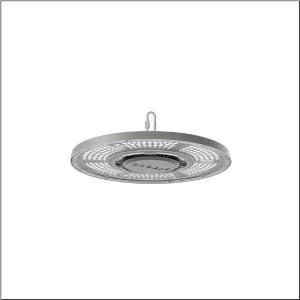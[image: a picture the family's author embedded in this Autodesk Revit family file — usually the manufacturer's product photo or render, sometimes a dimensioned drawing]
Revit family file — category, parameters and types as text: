
# Revit family: highbay_31-s_51hc427a4jmb
name_source: partatom
category: Lighting Fixtures
units: mm (PartAtom-declared; Revit-internal decimal feet)

## family parameters
Cut with Voids When Loaded = No
Host = Face
Light Source = No
Part Type = Normal
Room Calculation Point = No
Round Connector Dimension = Use Diameter
Shared = No

## types (1)
- Highbay 31-S (1 x LED, 20000 lm, 134 W, 4000K)
    Apparent Load = 134 VA
    CIE Flux Codes = 77 99 100 100 100
    Color Rendering = 80
    Color Temperature = 4000K
    Default Elevation = 1800 mm
    Description = Highbay 31-S, high bay luminaire, primary light control with lens, of PC, primary optical cover: cover panel, of PC, transparent, light emission: direct distribution, primary light characteristic: rotationally symmetric, installation type: suspended mounting, surface-mounted, LED, rated luminous flux: 20.000lm, luminous efficacy: 150lm/W, light colour: 840, colour temperature: 4000K, control gear: ON/OFF, with cable, 3x 1.0mm², free wire ends, mains connection: 220..240V, AC, 50/60Hz, cable length: 1,5m, rated input power: 134W, housing, rotationally symmetric, of diecast aluminium, powder-coated, grey aluminium (RAL 9007), with hook on luminaire side, incl. screw, diameter: 339mm, protection rating (complete): IP65, insulation class (complete): insulation class I (protective earthing), certification: CE, ENEC, UKCA, protection symbol: D, impact resistance: IK08, permissible operating ambient temperature: -30..+45°C, corresponds to IFS (International Featured Standards) requirements for safety and quality in the food industry, packaging unit: 1 piece
    Height = 141 mm
    Lamp = 1 x LED
    Lamp Light Flux = 20000 lm
    Lamp Power = 134 W
    Lamp count = 1
    Length = 339 mm
    Luminous efficacy = 149 lm/W
    Manufacturer = Siteco
    ModVariant = No
    Model = 51HC427A4JMB
    Mounting Place = Ceiling
    Mounting Type = Pendant
    Number of Poles = 1
    OnlyDefault = Yes
    Power Factor = 1
    Product Name = Highbay 31-S
    Product group = high bay luminaire
    ProductGroupID = 902
    Protection Class = Protection class I
    Protection Degree = IP 65
    RLX_Detail_Level = 1
    RLX_Emergency_Light_Flux = 0 lm
    RLX_Emergency_Type = 0
    RLX_Emergency_Type_DB = No
    RlxData = <blob elided: 161677 chars, md5=0884991c>
    Socket = socket
    Standby Power = 0 W
    System Light Flux = 20000 lm
    System Power = 134 W
    Type Comments = Product without accessories
    Type Image = l_1007237.jpg
    URL = http://relux.com
    VarID = ---
    Voltage = 0 V
    Weight = 0.00 kg
    Width = 0 mm  [stored 0 ft]

note: [stored X ft] marks values corroborated as IEEE doubles in the binary element streams (Revit-internal decimal feet)

## geometry (parser evidence)
native form markers: Blend x4, Sweep x12
no freeform markers — native parametric forms only
